# Revit family: Valve_Trim-DXV-Modulus-D35120500_Series
name_source: partatom
category: Plumbing Fixtures
units: mm (PartAtom-declared; Revit-internal decimal feet)

## family parameters
Cut with Voids When Loaded = No
Host = Face
OmniClass Number = 23.45.05.14.17
OmniClass Title = Showers
Part Type = Normal
Room Calculation Point = No
Round Connector Dimension = Use Diameter
Shared = Yes

## types (4) — shared parameters
ADA Compliant = Yes
ASME A112.18.1/CSA B125.1/ASSE 1016 = Yes
Assembly Code = D2010710
CW Connection = Yes
CWFU = 3
Cold Water Connection Diameter = 1/2"
Default Elevation = 44"
Description = DXV Modulus Pressure Balance Shower Valve Trim
Diameter = 7 7/16"
HW Connection = Yes
HWFU = 3
Height = 4 1/8"
Hot Water Connection Diameter = 1/2"
Installation Instruction Link = https://dxv01.blob.core.windows.net
Installation Type = Wall Mounted
Logo 2 = Yes
Manufacturer = DXV
Mounting Height = 48"
Price = Prices may vary. Please consult Manufacturer Representative for most up-to-date price list.
Product Documentation Link = https://dxv01.blob.core.windows.net
Product Page URL = https://www.dxv.com
Revised Date = 03/07/2022
Shower Rough Valve D35000500.191 = No
Tempered Water Connection Diameter = 1/2"
URL = https://www.dxv.com
Vent Connection = No
WFU = 4
Waste Connection = No
Width = 4 1/8"

## per-type parameters (varying)
| type | Finish | Material |
| D35120500.100 | Brass-DXV-100-Polished Chrome | Brass-DXV-100-Polished Chrome |
| D35120500.144 | Brass-DXV-144-Brushed Nickel | Brass-DXV-144-Brushed Nickel |
| D35120500.150 | Brass-DXV-150-Platinum Nickel | Brass-DXV-150-Platinum Nickel |
| D35120500.243 | Brass-DXV-243-Matte Black | Brass-DXV-243-Matte Black |

note: column(s) folded — value = type name in every type: Model

## geometry (parser evidence)
native form markers: Sweep x3
no freeform markers — native parametric forms only
